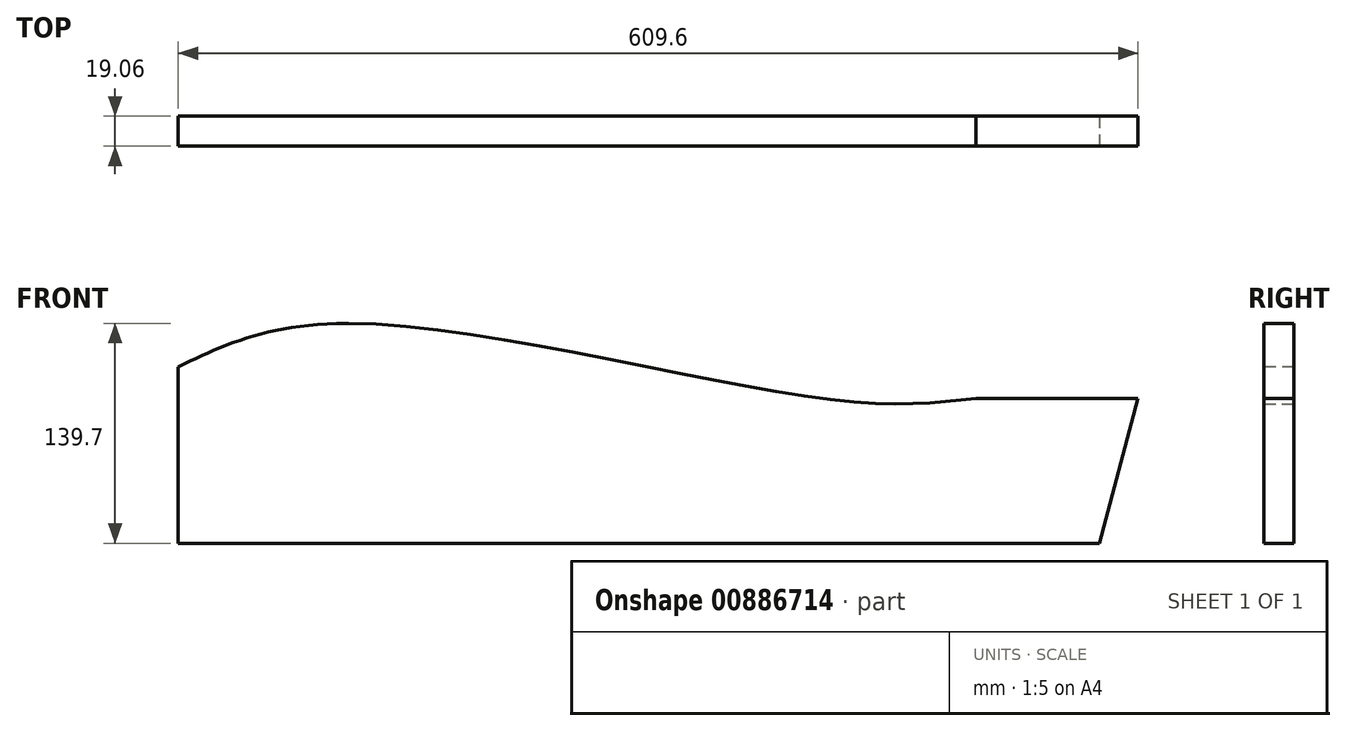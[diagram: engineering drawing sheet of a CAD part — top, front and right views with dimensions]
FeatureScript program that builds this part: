
annotation { "Feature Type Name" : "Feature", "Feature Type Description" : "" }
export const myFeature = defineFeature(function(context is Context, id is Id, definition is map)
    precondition{}
    {
        {
            var Q0;
            Q0=qCreatedBy(makeId("Right.planeOp"),FACE);
            var sketch = newSketch(context, id + "F0", { "sketchPlane" : qUnion([Q0])});
            skLineSegment(sketch, "E0.bottom", {"start": v(9.52, 69.85) * mm, "end": v(-9.52, 69.85) * mm});
            skLineSegment(sketch, "E0.top", {"start": v(9.52, -69.85) * mm, "end": v(-9.52, -69.85) * mm});
            skLineSegment(sketch, "E0.left", {"start": v(9.53, 69.85) * mm, "end": v(9.52, -69.85) * mm});
            skLineSegment(sketch, "E0.right", {"start": v(-9.52, 69.85) * mm, "end": v(-9.53, -69.85) * mm});
            skLineSegment(sketch, "E1", {"start": v(0, 0) * mm, "end": v(0, 98.92) * mm, "construction": true});
            skLineSegment(sketch, "E2", {"start": v(0, 0) * mm, "end": v(-99.13, 0) * mm, "construction": true});
            skSolve(sketch);
        }
        {
            var Q0;
            Q0=makeQuery(id+"F0.imprint","IMPRINT",FACE,{"disambiguationData":[TD([[makeQuery(id+"F0.imprint","IMPRINT",EDGE,{"derivedFrom":sQuery(id+"F0.wireOp",EDGE,"E0.bottom")}),1.0]])]});
            extrude(context, id + "F1", {"entities" : qUnion([Q0]), "endBound" : BoundingType.SYMMETRIC, "depth" : 609.6 * mm, "offsetDistance" : 25.4 * mm});
        }
        {
            var Q0;
            Q0=makeQuery(id+"F1.opExtrude","SWEPT_FACE",FACE,{"disambiguationData":[OSD([sQuery(id+"F0.wireOp",EDGE,"E0.right")])]});
            var sketch = newSketch(context, id + "F2", { "sketchPlane" : qUnion([Q0])});
            skLineSegment(sketch, "E3", {"start": v(304.8, 22.12) * mm, "end": v(304.8, 69.85) * mm});
            skLineSegment(sketch, "E4", {"start": v(304.8, 69.85) * mm, "end": v(-304.8, 69.85) * mm});
            skLineSegment(sketch, "E5", {"start": v(-304.8, 69.85) * mm, "end": v(-304.8, 42.27) * mm});
            skLineSegment(sketch, "E6", {"start": v(304.8, 22.12) * mm, "end": v(280.16, -69.85) * mm});
            skLineSegment(sketch, "E7", {"start": v(280.16, -69.85) * mm, "end": v(304.8, -69.85) * mm});
            skLineSegment(sketch, "E8", {"start": v(304.8, -69.85) * mm, "end": v(304.8, 22.12) * mm});
            skLineSegment(sketch, "E9", {"start": v(304.8, 22.12) * mm, "end": v(201.72, 22.12) * mm});
            skFitSpline(sketch, "E10", {"points": [v(201.72, 22.12) * mm, v(104.33, 22.12) * mm, v(-197.86, 69.85) * mm, v(-304.8, 42.27) * mm], "startDerivative": vector(-300.7, -33.4) * mm, "endDerivative": vector(-310.6, -148.55) * mm});
            skSolve(sketch);
        }
        {
            var Q0;
            {var subQ0=sQuery(id+"F2.wireOp",EDGE,"E5");Q0=makeQuery(id+"F2.imprint","IMPRINT",FACE,{"disambiguationData":[TD([[makeQuery(id+"F2.imprint","IMPRINT",EDGE,{"derivedFrom":subQ0}),1.0]])]});}
            var Q1;
            {var subQ0=sQuery(id+"F2.wireOp",EDGE,"E3");Q1=makeQuery(id+"F2.imprint","IMPRINT",FACE,{"disambiguationData":[TD([[makeQuery(id+"F2.imprint","IMPRINT",EDGE,{"derivedFrom":subQ0}),-1.0]])]});}
            var Q2;
            Q2=makeQuery(id+"F2.imprint","IMPRINT",FACE,{"disambiguationData":[TD([[makeQuery(id+"F2.imprint","IMPRINT",EDGE,{"derivedFrom":sQuery(id+"F2.wireOp",EDGE,"E6")}),1.0]])]});
            extrude(context, id + "F3", {"entities" : qUnion([Q0, Q1, Q2]), "operationType" : NewBodyOperationType.REMOVE, "endBound" : BoundingType.THROUGH_ALL, "oppositeDirection" : true, "depth" : 25.4 * mm, "offsetDistance" : 25.4 * mm});
        }
    });
